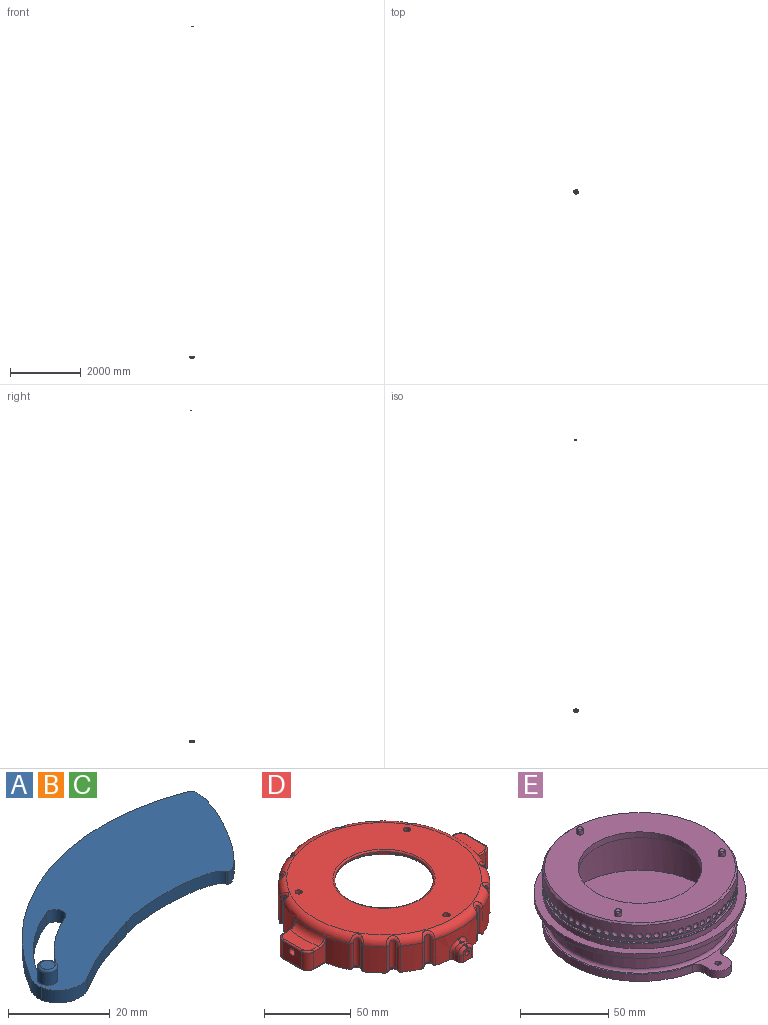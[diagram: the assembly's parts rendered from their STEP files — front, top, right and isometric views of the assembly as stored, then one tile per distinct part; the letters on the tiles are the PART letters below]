
ASSEMBLY  parts=5 mates=6
PART A: 17 faces, bbox 68.7x35.4x6.5 mm
  f0: extruded ~26.08x3.35mm, area 81.3mm2, adj f3,f4,f8,f16
  f1: extruded ~24.8x14.67mm, area 90.9mm2, adj f2,f3,f4,f8
  f2: cylinder r=54.5mm len=67.29mm, axis (0,0,-1), area 232.4mm2, adj f1,f3,f4,f14
  f3: plane 68.73x35.38mm, normal (0,0,1), area 1340.6mm2, adj f0,f1,f2,f5,f7,f8,f9,f10
  f4: plane 68.73x35.38mm, normal (0,0,-1), area 1353.2mm2, adj f0,f1,f2,f7,f8,f9,f10,f11
  f5: cylinder r=2mm len=4mm, axis (0,0,-1), area 37.7mm2, adj f3,f13
  f6: plane 3x3mm, normal (0,0,1), area 7.1mm2, adj f13
  f7: extruded ~14.32x6.42mm, area 47.2mm2, adj f3,f4,f15,f16
  f8: cylinder r=0.3mm len=3mm, axis (0,0,-1), area 1mm2, adj f0,f1,f3,f4
  f9: cylinder r=32.5mm len=14.49mm, axis (0,0,1), area 56.5mm2, adj f3,f4,f10,f12
  f10: cylinder r=2.05mm len=3.74mm, axis (0,0,1), area 19.3mm2, adj f3,f4,f9,f11
  f11: cylinder r=28.4mm len=12.66mm, axis (0,0,1), area 49.4mm2, adj f3,f4,f10,f12
  f12: cylinder r=2.05mm len=3.95mm, axis (0,0,1), area 19.3mm2, adj f3,f4,f9,f11
  f13: torus R=1.5mm, axis (0,0,1), area 9mm2, adj f5,f6
  f14: cylinder r=6mm len=3.7mm, axis (0,0,-1), area 11.6mm2, adj f2,f3,f4,f15
  f15: cylinder r=6mm len=9.02mm, axis (0,0,1), area 34.5mm2, adj f3,f4,f7,f14
  f16: cylinder r=60mm len=4.4mm, axis (0,0,-1), area 13.9mm2, adj f0,f3,f4,f7
PART B: same geometry as A
PART C: same geometry as A
PART D: 203 faces, bbox 150.8x136x23.4 mm
  f0: cylinder r=2.15mm len=12.4mm, axis (1,0,0), area 167.5mm2, adj f31,f172
  f1: plane 53.71x23.5mm, normal (0,0,-1), area 489.7mm2, adj f21,f28,f34,f107,f122,f162,f163,f166
  f2: cylinder r=2.15mm len=12.4mm, axis (1,0,0), area 167.5mm2, adj f31,f166
  f3: plane 53.71x23.5mm, normal (0,0,-1), area 489.7mm2, adj f15,f27,f34,f137,f152,f168,f171,f172
  f4: plane 13.56x12.34mm, normal (0,0,-1), area 52.7mm2, adj f8,f34,f148,f152
  f5: plane 14.36x10.74mm, normal (0,0,-1), area 52.7mm2, adj f7,f34,f144,f148
  f6: cylinder r=61.2mm len=34.07mm, axis (0,0,-1), area 481mm2, adj f12,f18,f71,f72,f73,f74,f75,f114
  f7: cylinder r=61.2mm len=18.4mm, axis (0,0,-1), area 242.2mm2, adj f5,f12,f144,f145,f148,f150
  f8: cylinder r=61.2mm len=18.4mm, axis (0,0,-1), area 242.2mm2, adj f4,f12,f148,f149,f152,f154
  f9: plane 13.56x12.34mm, normal (0,0,-1), area 52.7mm2, adj f14,f34,f133,f137
  f10: plane 14.36x10.74mm, normal (0,0,-1), area 52.7mm2, adj f13,f34,f129,f133
  f11: plane 35.36x13.6mm, normal (0,0,-1), area 196.5mm2, adj f23,f34,f39,f40,f41,f45,f46,f49
  f12: torus R=56.2mm, axis (0,0,1), area 2369.6mm2, adj f6,f7,f8,f13,f14,f15,f19,f20
  f13: cylinder r=61.2mm len=18.4mm, axis (0,0,-1), area 242.2mm2, adj f10,f12,f129,f130,f133,f135
  f14: cylinder r=61.2mm len=18.4mm, axis (0,0,-1), area 242.2mm2, adj f9,f12,f133,f134,f137,f139
  f15: cylinder r=61.2mm len=18.4mm, axis (0,0,-1), area 283.5mm2, adj f3,f12,f82,f137,f138,f180,f185
  f16: plane 13.56x12.34mm, normal (0,0,-1), area 52.7mm2, adj f20,f34,f118,f122
  f17: plane 14.36x10.74mm, normal (0,0,-1), area 52.7mm2, adj f19,f34,f114,f118
  f18: plane 35.36x13.6mm, normal (0,0,-1), area 196.5mm2, adj f6,f34,f35,f36,f37,f63,f64,f67
  f19: cylinder r=61.2mm len=18.4mm, axis (0,0,-1), area 242.2mm2, adj f12,f17,f114,f115,f118,f120
  f20: cylinder r=61.2mm len=18.4mm, axis (0,0,-1), area 242.2mm2, adj f12,f16,f118,f119,f122,f124
  f21: cylinder r=61.2mm len=18.4mm, axis (0,0,-1), area 283.5mm2, adj f1,f12,f87,f122,f123,f186,f191
  f22: plane 13.56x12.34mm, normal (0,0,-1), area 52.7mm2, adj f25,f34,f103,f107
  f23: cylinder r=61.2mm len=34.07mm, axis (0,0,-1), area 481mm2, adj f11,f12,f53,f54,f55,f56,f57,f99
  f24: cylinder r=61.2mm len=18.4mm, axis (0,0,-1), area 242.2mm2, adj f12,f26,f99,f100,f103,f105
  f25: cylinder r=61.2mm len=18.4mm, axis (0,0,-1), area 242.2mm2, adj f12,f22,f103,f104,f107,f109
  f26: plane 14.36x10.74mm, normal (0,0,-1), area 52.7mm2, adj f24,f34,f99,f103
  f27: cylinder r=61.2mm len=18.4mm, axis (0,0,-1), area 283.5mm2, adj f3,f12,f84,f152,f153,f174,f181
  f28: cylinder r=61.2mm len=18.4mm, axis (0,0,-1), area 283.5mm2, adj f1,f12,f86,f107,f108,f190,f197
  f29: cylinder r=1.75mm len=6.3mm, axis (0,-1,0), area 69.3mm2, adj f31,f67
  f30: cylinder r=1.75mm len=6.3mm, axis (0,-1,0), area 69.3mm2, adj f31,f49
  f31: cylinder r=55.2mm len=110.4mm, axis (0,0,-1), area 6264mm2, adj f0,f2,f29,f30,f34,f81
  f32: plane 110x110mm, normal (0,0,-1), area 6705.6mm2, adj f81,f198,f200,f201,f202
  f33: plane 112.4x112.4mm, normal (0,0,1), area 7147mm2, adj f12,f157,f158,f159,f199
  f34: cone r=57.2mm half-angle=45deg, axis (0,0,-1), area 998.8mm2, adj f1,f3,f4,f5,f9,f10,f11,f16
  f35: plane 5x3.25mm, normal (-1,0,0), area 16.2mm2, adj f18,f70,f75,f80
  f36: plane 5x3.25mm, normal (1,0,0), area 16.2mm2, adj f18,f69,f71,f76
  f37: plane 8x7mm, normal (0,1,0), area 42.5mm2, adj f18,f44,f76,f77,f78,f79,f80
  f38: plane 2.8x1mm, normal (0,0,1), area 2.8mm2, adj f69,f70,f73,f78
  f39: plane 5x3.25mm, normal (-1,0,0), area 16.2mm2, adj f11,f52,f57,f58
  f40: plane 8x7mm, normal (0,-1,0), area 42.5mm2, adj f11,f43,f58,f59,f60,f61,f62
  f41: plane 5x3.25mm, normal (1,0,0), area 16.2mm2, adj f11,f51,f53,f62
  f42: plane 2.8x1mm, normal (0,0,1), area 2.8mm2, adj f51,f52,f55,f60
  f43: cylinder r=1.75mm len=4mm, axis (0,-1,0), area 44mm2, adj f40,f50
  f44: cylinder r=1.75mm len=4mm, axis (0,-1,0), area 44mm2, adj f37,f68
  f45: plane 6.63x2.5mm, normal (1,0,0), area 16.6mm2, adj f11,f48,f49,f50
  f46: plane 6.63x2.5mm, normal (-1,0,0), area 16.6mm2, adj f11,f47,f49,f50
  f47: plane 2.83x2.5mm, normal (-0.5,0,-0.87), area 8.2mm2, adj f46,f48,f49,f50
  f48: plane 2.83x2.5mm, normal (0.5,0,-0.87), area 8.2mm2, adj f45,f47,f49,f50
  f49: plane 8.26x5.65mm, normal (0,-1,0), area 32.5mm2, adj f11,f30,f45,f46,f47,f48
  f50: plane 8.26x5.65mm, normal (0,1,0), area 32.5mm2, adj f11,f43,f45,f46,f47,f48
  f51: cylinder r=5mm len=5mm, axis (0,-1,0), area 23.8mm2, adj f41,f42,f54,f61
  f52: cylinder r=5mm len=5mm, axis (0,1,0), area 23.8mm2, adj f39,f42,f56,f59
  f53: cylinder r=2mm len=5mm, axis (0,0,-1), area 14.5mm2, adj f11,f23,f41,f54
  f54: bspline ~8.56x8.28mm, area 27mm2, adj f23,f51,f53,f55
  f55: torus R=63.2mm, axis (0,0,1), area 3.1mm2, adj f23,f42,f54,f56
  f56: bspline ~8.56x8.28mm, area 27mm2, adj f23,f52,f55,f57
  f57: cylinder r=2mm len=5mm, axis (0,0,-1), area 14.5mm2, adj f11,f23,f39,f56
  f58: cylinder r=2mm len=5mm, axis (0,0,1), area 15.7mm2, adj f11,f39,f40,f59
  f59: torus R=3mm, axis (0,1,0), area 21.1mm2, adj f40,f52,f58,f60
  f60: cylinder r=2mm len=2mm, axis (-1,0,0), area 3.1mm2, adj f40,f42,f59,f61
  f61: torus R=3mm, axis (0,1,0), area 21.1mm2, adj f40,f51,f60,f62
  f62: cylinder r=2mm len=5mm, axis (0,0,-1), area 15.7mm2, adj f11,f40,f41,f61
  f63: plane 6.63x2.5mm, normal (-1,0,0), area 16.6mm2, adj f18,f66,f67,f68
  f64: plane 6.63x2.5mm, normal (1,0,0), area 16.6mm2, adj f18,f65,f67,f68
  f65: plane 2.83x2.5mm, normal (0.5,0,-0.87), area 8.2mm2, adj f64,f66,f67,f68
  f66: plane 2.83x2.5mm, normal (-0.5,0,-0.87), area 8.2mm2, adj f63,f65,f67,f68
  f67: plane 8.26x5.65mm, normal (0,1,0), area 32.5mm2, adj f18,f29,f63,f64,f65,f66
  f68: plane 8.26x5.65mm, normal (0,-1,0), area 32.5mm2, adj f18,f44,f63,f64,f65,f66
  f69: cylinder r=5mm len=5mm, axis (0,-1,0), area 23.8mm2, adj f36,f38,f72,f77
  f70: cylinder r=5mm len=5mm, axis (0,1,0), area 23.8mm2, adj f35,f38,f74,f79
  f71: cylinder r=2mm len=5mm, axis (0,0,-1), area 14.5mm2, adj f6,f18,f36,f72
  f72: bspline ~8.28x7.4mm, area 27mm2, adj f6,f69,f71,f73
  f73: torus R=63.2mm, axis (0,0,1), area 3.1mm2, adj f6,f38,f72,f74
  f74: bspline ~8.56x8.28mm, area 27mm2, adj f6,f70,f73,f75
  f75: cylinder r=2mm len=5mm, axis (0,0,-1), area 14.5mm2, adj f6,f18,f35,f74
  f76: cylinder r=2mm len=5mm, axis (0,0,1), area 15.7mm2, adj f18,f36,f37,f77
  f77: torus R=3mm, axis (0,1,0), area 21.1mm2, adj f37,f69,f76,f78
  f78: cylinder r=2mm len=2mm, axis (1,0,0), area 3.1mm2, adj f37,f38,f77,f79
  f79: torus R=3mm, axis (0,1,0), area 21.1mm2, adj f37,f70,f78,f80
  f80: cylinder r=2mm len=5mm, axis (0,0,-1), area 15.7mm2, adj f18,f35,f37,f79
  f81: cone r=55.2mm half-angle=45deg, axis (0,0,-1), area 97.9mm2, adj f31,f32
  f82: plane 14.97x10.09mm, normal (0,-1,0), area 125.6mm2, adj f15,f93,f179,f180,f185
  f83: plane 15x12mm, normal (-1,0,0), area 165.5mm2, adj f92,f93,f161,f177,f183
  f84: plane 14.97x10.09mm, normal (0,1,0), area 125.6mm2, adj f27,f92,f174,f175,f181
  f85: plane 23x8.83mm, normal (0,0,1), area 180.6mm2, adj f95,f175,f176,f177,f178,f179
  f86: plane 14.97x10.09mm, normal (0,-1,0), area 125.6mm2, adj f28,f91,f190,f196,f197
  f87: plane 14.97x10.09mm, normal (0,1,0), area 125.6mm2, adj f21,f90,f186,f191,f192
  f88: plane 15x12mm, normal (1,0,0), area 165.5mm2, adj f90,f91,f160,f188,f194
  f89: plane 23x8.83mm, normal (0,0,1), area 180.6mm2, adj f94,f192,f193,f194,f195,f196
  f90: cylinder r=5mm len=12mm, axis (0,0,1), area 94.2mm2, adj f87,f88,f187,f193
  f91: cylinder r=5mm len=12mm, axis (0,0,-1), area 94.2mm2, adj f86,f88,f189,f195
  f92: cylinder r=5mm len=12mm, axis (0,0,-1), area 94.2mm2, adj f83,f84,f176,f182
  f93: cylinder r=5mm len=12mm, axis (0,0,1), area 94.2mm2, adj f82,f83,f178,f184
  f94: torus R=66.18mm, axis (0,0,-1), area 174.7mm2, adj f12,f89,f191,f197
  f95: torus R=66.18mm, axis (0,0,-1), area 174.7mm2, adj f12,f85,f174,f180
  f96: cylinder r=2.5mm len=19.36mm, axis (0,0,-1), area 101.7mm2, adj f107,f108,f109,f110
  f97: cylinder r=2.5mm len=19.36mm, axis (0,0,-1), area 101.7mm2, adj f103,f104,f105,f106
  f98: cylinder r=2.5mm len=19.36mm, axis (0,0,-1), area 101.7mm2, adj f99,f100,f101,f102
  f99: torus R=4.5mm, axis (0,0,1), area 27.7mm2, adj f11,f23,f24,f26,f34,f98,f100,f101
  f100: cylinder r=2mm len=18.36mm, axis (0,0,1), area 39.8mm2, adj f24,f98,f99,f102
  f101: cylinder r=2mm len=18.36mm, axis (0,0,1), area 39.8mm2, adj f23,f98,f99,f102
  f102: bspline ~7.7x5.94mm, area 31.7mm2, adj f12,f98,f100,f101
  f103: torus R=4.5mm, axis (0,0,1), area 27.7mm2, adj f22,f24,f25,f26,f34,f97,f104,f105
  f104: cylinder r=2mm len=18.36mm, axis (0,0,1), area 39.8mm2, adj f25,f97,f103,f106
  f105: cylinder r=2mm len=18.36mm, axis (0,0,1), area 39.8mm2, adj f24,f97,f103,f106
  f106: bspline ~6.84x6.41mm, area 31.7mm2, adj f12,f97,f104,f105
  f107: torus R=4.5mm, axis (0,0,1), area 27.7mm2, adj f1,f22,f25,f28,f34,f96,f108,f109
  f108: cylinder r=2mm len=18.36mm, axis (0,0,1), area 39.8mm2, adj f28,f96,f107,f110
  f109: cylinder r=2mm len=18.36mm, axis (0,0,1), area 39.8mm2, adj f25,f96,f107,f110
  f110: bspline ~7.26x5.94mm, area 31.7mm2, adj f12,f96,f108,f109
  f111: cylinder r=2.5mm len=19.36mm, axis (0,0,-1), area 101.7mm2, adj f122,f123,f124,f125
  f112: cylinder r=2.5mm len=19.36mm, axis (0,0,-1), area 101.7mm2, adj f118,f119,f120,f121
  f113: cylinder r=2.5mm len=19.36mm, axis (0,0,-1), area 101.7mm2, adj f114,f115,f116,f117
  f114: torus R=4.5mm, axis (0,0,1), area 27.7mm2, adj f6,f17,f18,f19,f34,f113,f115,f116
  f115: cylinder r=2mm len=18.36mm, axis (0,0,1), area 39.8mm2, adj f19,f113,f114,f117
  f116: cylinder r=2mm len=18.36mm, axis (0,0,1), area 39.8mm2, adj f6,f113,f114,f117
  f117: bspline ~7.7x5.93mm, area 31.7mm2, adj f12,f113,f115,f116
  f118: torus R=4.5mm, axis (0,0,1), area 27.7mm2, adj f16,f17,f19,f20,f34,f112,f119,f120
  f119: cylinder r=2mm len=18.36mm, axis (0,0,1), area 39.8mm2, adj f20,f112,f118,f121
  f120: cylinder r=2mm len=18.36mm, axis (0,0,1), area 39.8mm2, adj f19,f112,f118,f121
  f121: bspline ~6.85x6.41mm, area 31.7mm2, adj f12,f112,f119,f120
  f122: torus R=4.5mm, axis (0,0,1), area 27.7mm2, adj f1,f16,f20,f21,f34,f111,f123,f124
  f123: cylinder r=2mm len=18.36mm, axis (0,0,1), area 39.8mm2, adj f21,f111,f122,f125
  f124: cylinder r=2mm len=18.36mm, axis (0,0,1), area 39.8mm2, adj f20,f111,f122,f125
  f125: bspline ~7.26x5.94mm, area 31.7mm2, adj f12,f111,f123,f124
  f126: cylinder r=2.5mm len=19.36mm, axis (0,0,-1), area 101.7mm2, adj f137,f138,f139,f140
  f127: cylinder r=2.5mm len=19.36mm, axis (0,0,-1), area 101.7mm2, adj f133,f134,f135,f136
  f128: cylinder r=2.5mm len=19.36mm, axis (0,0,-1), area 101.7mm2, adj f129,f130,f131,f132
  f129: torus R=4.5mm, axis (0,0,1), area 27.7mm2, adj f10,f11,f13,f23,f34,f128,f130,f131
  f130: cylinder r=2mm len=18.36mm, axis (0,0,1), area 39.8mm2, adj f13,f128,f129,f132
  f131: cylinder r=2mm len=18.36mm, axis (0,0,1), area 39.8mm2, adj f23,f128,f129,f132
  f132: bspline ~7.7x5.93mm, area 31.7mm2, adj f12,f128,f130,f131
  f133: torus R=4.5mm, axis (0,0,1), area 27.7mm2, adj f9,f10,f13,f14,f34,f127,f134,f135
  f134: cylinder r=2mm len=18.36mm, axis (0,0,1), area 39.8mm2, adj f14,f127,f133,f136
  f135: cylinder r=2mm len=18.36mm, axis (0,0,1), area 39.8mm2, adj f13,f127,f133,f136
  f136: bspline ~6.85x6.41mm, area 31.7mm2, adj f12,f127,f134,f135
  f137: torus R=4.5mm, axis (0,0,1), area 27.7mm2, adj f3,f9,f14,f15,f34,f126,f138,f139
  f138: cylinder r=2mm len=18.36mm, axis (0,0,1), area 39.8mm2, adj f15,f126,f137,f140
  f139: cylinder r=2mm len=18.36mm, axis (0,0,1), area 39.8mm2, adj f14,f126,f137,f140
  f140: bspline ~7.26x5.93mm, area 31.7mm2, adj f12,f126,f138,f139
  f141: cylinder r=2.5mm len=19.36mm, axis (0,0,-1), area 101.7mm2, adj f152,f153,f154,f155
  f142: cylinder r=2.5mm len=19.36mm, axis (0,0,-1), area 101.7mm2, adj f148,f149,f150,f151
  f143: cylinder r=2.5mm len=19.36mm, axis (0,0,-1), area 101.7mm2, adj f144,f145,f146,f147
  f144: torus R=4.5mm, axis (0,0,1), area 27.7mm2, adj f5,f6,f7,f18,f34,f143,f145,f146
  f145: cylinder r=2mm len=18.36mm, axis (0,0,1), area 39.8mm2, adj f7,f143,f144,f147
  f146: cylinder r=2mm len=18.36mm, axis (0,0,1), area 39.8mm2, adj f6,f143,f144,f147
  f147: bspline ~7.7x5.94mm, area 31.7mm2, adj f12,f143,f145,f146
  f148: torus R=4.5mm, axis (0,0,1), area 27.7mm2, adj f4,f5,f7,f8,f34,f142,f149,f150
  f149: cylinder r=2mm len=18.36mm, axis (0,0,1), area 39.8mm2, adj f8,f142,f148,f151
  f150: cylinder r=2mm len=18.36mm, axis (0,0,1), area 39.8mm2, adj f7,f142,f148,f151
  f151: bspline ~6.84x6.41mm, area 31.7mm2, adj f12,f142,f149,f150
  f152: torus R=4.5mm, axis (0,0,1), area 27.7mm2, adj f3,f4,f8,f27,f34,f141,f153,f154
  f153: cylinder r=2mm len=18.36mm, axis (0,0,1), area 39.8mm2, adj f27,f141,f152,f155
  f154: cylinder r=2mm len=18.36mm, axis (0,0,1), area 39.8mm2, adj f8,f141,f152,f155
  f155: bspline ~7.26x5.94mm, area 31.7mm2, adj f12,f141,f153,f154
  f156: cylinder r=28.5mm len=57mm, axis (0,0,1), area 179.1mm2, adj f198,f199
  f157: cylinder r=2.1mm len=4.2mm, axis (0,0,1), area 33mm2, adj f33,f202
  f158: cylinder r=2.1mm len=4.2mm, axis (0,0,1), area 33mm2, adj f33,f200
  f159: cylinder r=2.1mm len=4.2mm, axis (0,0,1), area 33mm2, adj f33,f201
  f160: cylinder r=2.15mm len=4.3mm, axis (1,0,0), area 54mm2, adj f88,f167
  f161: cylinder r=2.15mm len=4.3mm, axis (1,0,0), area 54mm2, adj f83,f173
  f162: plane 11.05x3.4mm, normal (0,1,0), area 37.6mm2, adj f1,f165,f166,f167
  f163: plane 11.05x3.4mm, normal (0,-1,0), area 37.6mm2, adj f1,f164,f166,f167
  f164: plane 3.55x3.4mm, normal (0,-0.5,-0.87), area 13.9mm2, adj f163,f165,f166,f167
  f165: plane 3.55x3.4mm, normal (0,0.5,-0.87), area 13.9mm2, adj f162,f164,f166,f167
  f166: plane 13.1x7.1mm, normal (1,0,0), area 71.2mm2, adj f1,f2,f162,f163,f164,f165
  f167: plane 13.1x7.1mm, normal (-1,0,0), area 71.2mm2, adj f1,f160,f162,f163,f164,f165
  f168: plane 11.05x3.4mm, normal (0,1,0), area 37.6mm2, adj f3,f169,f172,f173
  f169: plane 3.55x3.4mm, normal (0,0.5,-0.87), area 13.9mm2, adj f168,f170,f172,f173
  f170: plane 3.55x3.4mm, normal (0,-0.5,-0.87), area 13.9mm2, adj f169,f171,f172,f173
  f171: plane 11.05x3.4mm, normal (0,-1,0), area 37.6mm2, adj f3,f170,f172,f173
  f172: plane 13.1x7.1mm, normal (-1,0,0), area 71.2mm2, adj f0,f3,f168,f169,f170,f171
  f173: plane 13.1x7.1mm, normal (1,0,0), area 71.2mm2, adj f3,f161,f168,f169,f170,f171
  f174: bspline ~7.48x6.11mm, area 10.2mm2, adj f12,f27,f84,f95,f175
  f175: cylinder r=1mm len=4.83mm, axis (-1,0,0), area 7.6mm2, adj f84,f85,f174,f176
  f176: torus R=4mm, axis (0,0,-1), area 11.4mm2, adj f85,f92,f175,f177
  f177: cylinder r=1mm len=15mm, axis (0,-1,0), area 23.6mm2, adj f83,f85,f176,f178
  f178: torus R=4mm, axis (0,0,-1), area 11.4mm2, adj f85,f93,f177,f179
  f179: cylinder r=1mm len=4.83mm, axis (1,0,0), area 7.6mm2, adj f82,f85,f178,f180
  f180: bspline ~7.48x6.11mm, area 10.2mm2, adj f12,f15,f82,f95,f179
  f181: cylinder r=1mm len=10.09mm, axis (-1,0,0), area 15.7mm2, adj f3,f27,f84,f182
  f182: torus R=4mm, axis (0,0,1), area 11.4mm2, adj f3,f92,f181,f183
  f183: cylinder r=1mm len=15mm, axis (0,-1,0), area 23.6mm2, adj f3,f83,f182,f184
  f184: torus R=4mm, axis (0,0,1), area 11.4mm2, adj f3,f93,f183,f185
  f185: cylinder r=1mm len=10.09mm, axis (1,0,0), area 15.7mm2, adj f3,f15,f82,f184
  f186: cylinder r=1mm len=10.09mm, axis (-1,0,0), area 15.7mm2, adj f1,f21,f87,f187
  f187: torus R=4mm, axis (0,0,1), area 11.4mm2, adj f1,f90,f186,f188
  f188: cylinder r=1mm len=15mm, axis (0,1,0), area 23.6mm2, adj f1,f88,f187,f189
  f189: torus R=4mm, axis (0,0,1), area 11.4mm2, adj f1,f91,f188,f190
  f190: cylinder r=1mm len=10.09mm, axis (1,0,0), area 15.7mm2, adj f1,f28,f86,f189
  f191: bspline ~7.48x6.11mm, area 10.2mm2, adj f12,f21,f87,f94,f192
  f192: cylinder r=1mm len=4.83mm, axis (-1,0,0), area 7.6mm2, adj f87,f89,f191,f193
  f193: torus R=4mm, axis (0,0,-1), area 11.4mm2, adj f89,f90,f192,f194
  f194: cylinder r=1mm len=15mm, axis (0,1,0), area 23.6mm2, adj f88,f89,f193,f195
  f195: torus R=4mm, axis (0,0,-1), area 11.4mm2, adj f89,f91,f194,f196
  f196: cylinder r=1mm len=4.83mm, axis (1,0,0), area 7.6mm2, adj f86,f89,f195,f197
  f197: bspline ~7.48x6.11mm, area 10.2mm2, adj f12,f28,f86,f94,f196
  f198: torus R=29.5mm, axis (0,0,1), area 284.9mm2, adj f32,f156
  f199: torus R=29.5mm, axis (0,0,1), area 284.9mm2, adj f33,f156
  f200: cone r=2.6mm half-angle=45deg, axis (0,0,-1), area 10.4mm2, adj f32,f158
  f201: cone r=2.6mm half-angle=45deg, axis (0,0,-1), area 10.4mm2, adj f32,f159
  f202: cone r=2.6mm half-angle=45deg, axis (0,0,-1), area 10.4mm2, adj f32,f157
PART E: 116 faces, bbox 120x140x43.2 mm
  f0: plane 108x108mm, normal (0,0,1), area 5274.7mm2, adj f8,f103,f106,f109,f112
  f1: cylinder r=55mm len=110mm, axis (0,0,-1), area 1226.8mm2, adj f4,f10
  f2: cylinder r=60mm len=120mm, axis (0,0,1), area 1131mm2, adj f3,f4
  f3: plane 120x120mm, normal (0,0,-1), area 2148.8mm2, adj f2,f29
  f4: plane 120x120mm, normal (0,0,1), area 1806.4mm2, adj f1,f2
  f5: plane 109.6x109.6mm, normal (0,0,-1), area 358.1mm2, adj f6,f11
  f6: cylinder r=53.75mm len=107.5mm, axis (0,0,1), area 844.3mm2, adj f5,f7
  f7: plane 109.6x109.6mm, normal (0,0,1), area 358.1mm2, adj f6,f10
  f8: cone r=54mm half-angle=45deg, axis (0,0,-1), area 484.3mm2, adj f0,f9
  f9: cylinder r=55mm len=110mm, axis (0,0,-1), area 2746.1mm2, adj f8,f11,f31,f32,f33,f34,f35,f36
  f10: cone r=54.8mm half-angle=45deg, axis (0,0,-1), area 97.6mm2, adj f1,f7
  f11: cone r=55mm half-angle=45deg, axis (0,0,1), area 97.6mm2, adj f5,f9
  f12: cylinder r=52mm len=104mm, axis (0,0,-1), area 3463.3mm2, adj f29,f30
  f13: plane 5x3.82mm, normal (-1,0,0), area 19.1mm2, adj f14,f17,f25,f26
  f14: cylinder r=7.5mm len=15mm, axis (0,0,-1), area 117.8mm2, adj f13,f15,f25,f26
  f15: plane 5x3.82mm, normal (1,0,0), area 19.1mm2, adj f14,f23,f25,f26
  f16: cylinder r=1.75mm len=5mm, axis (0,0,-1), area 55mm2, adj f25,f26
  f17: cylinder r=5mm len=5mm, axis (0,0,-1), area 34mm2, adj f13,f24,f25,f26
  f18: cylinder r=5mm len=5mm, axis (0,0,-1), area 34mm2, adj f21,f24,f25,f26
  f19: plane 5x3.82mm, normal (1,0,0), area 19.1mm2, adj f20,f25,f26,f27
  f20: cylinder r=7.5mm len=15mm, axis (0,0,-1), area 117.8mm2, adj f19,f21,f25,f26
  f21: plane 5x3.82mm, normal (-1,0,0), area 19.1mm2, adj f18,f20,f25,f26
  f22: cylinder r=1.75mm len=5mm, axis (0,0,-1), area 55mm2, adj f25,f26
  f23: cylinder r=5mm len=5mm, axis (0,0,-1), area 34mm2, adj f15,f25,f26,f28
  f24: cylinder r=55mm len=107.59mm, axis (0,0,-1), area 748.5mm2, adj f17,f18,f25,f26
  f25: plane 140x110mm, normal (0,0,-1), area 9904.6mm2, adj f13,f14,f15,f16,f17,f18,f19,f20
  f26: plane 140x110mm, normal (0,0,1), area 743.7mm2, adj f13,f14,f15,f16,f17,f18,f19,f20
  f27: cylinder r=5mm len=5mm, axis (0,0,-1), area 34mm2, adj f19,f25,f26,f28
  f28: cylinder r=55mm len=107.59mm, axis (0,0,-1), area 748.5mm2, adj f23,f25,f26,f27
  f29: torus R=54mm, axis (0,0,-1), area 1040.8mm2, adj f3,f12
  f30: torus R=54mm, axis (0,0,-1), area 1040.8mm2, adj f12,f26
  f31: sphere r=1.75mm, area 19.1mm2, adj f9
  f32: sphere r=1.75mm, area 19.1mm2, adj f9
  f33: sphere r=1.75mm, area 20.8mm2, adj f9
  f34: sphere r=1.75mm, area 19.1mm2, adj f9
  f35: sphere r=1.75mm, area 19.2mm2, adj f9
  f36: sphere r=1.75mm, area 20.8mm2, adj f9
  f37: sphere r=1.75mm, area 19.1mm2, adj f9
  f38: sphere r=1.75mm, area 20.8mm2, adj f9
  f39: sphere r=1.75mm, area 19.2mm2, adj f9
  f40: sphere r=1.75mm, area 20.8mm2, adj f9
  f41: sphere r=1.75mm, area 19.2mm2, adj f9
  f42: sphere r=1.75mm, area 20.8mm2, adj f9
  f43: sphere r=1.75mm, area 20.8mm2, adj f9
  f44: sphere r=1.75mm, area 19.1mm2, adj f9
  f45: sphere r=1.75mm, area 19.1mm2, adj f9
  f46: sphere r=1.75mm, area 20.8mm2, adj f9
  f47: sphere r=1.75mm, area 20.8mm2, adj f9
  f48: sphere r=1.75mm, area 19.1mm2, adj f9
  f49: sphere r=1.75mm, area 19.1mm2, adj f9
  f50: sphere r=1.75mm, area 19.1mm2, adj f9
  f51: sphere r=1.75mm, area 20.8mm2, adj f9
  f52: sphere r=1.75mm, area 19.1mm2, adj f9
  f53: sphere r=1.75mm, area 19.2mm2, adj f9
  f54: sphere r=1.75mm, area 20.8mm2, adj f9
  f55: sphere r=1.75mm, area 19.1mm2, adj f9
  f56: sphere r=1.75mm, area 20.8mm2, adj f9
  f57: sphere r=1.75mm, area 19.2mm2, adj f9
  f58: sphere r=1.75mm, area 20.8mm2, adj f9
  f59: sphere r=1.75mm, area 19.2mm2, adj f9
  f60: sphere r=1.75mm, area 20.8mm2, adj f9
  f61: sphere r=1.75mm, area 20.8mm2, adj f9
  f62: sphere r=1.75mm, area 19.1mm2, adj f9
  f63: sphere r=1.75mm, area 19.1mm2, adj f9
  f64: sphere r=1.75mm, area 20.8mm2, adj f9
  f65: sphere r=1.75mm, area 20.8mm2, adj f9
  f66: sphere r=1.75mm, area 19.1mm2, adj f9
  f67: sphere r=1.75mm, area 19.1mm2, adj f9
  f68: sphere r=1.75mm, area 19.1mm2, adj f9
  f69: sphere r=1.75mm, area 20.8mm2, adj f9
  f70: sphere r=1.75mm, area 20.8mm2, adj f9
  f71: sphere r=1.75mm, area 19.1mm2, adj f9
  f72: sphere r=1.75mm, area 19.1mm2, adj f9
  f73: sphere r=1.75mm, area 20.8mm2, adj f9
  f74: sphere r=1.75mm, area 20.8mm2, adj f9
  f75: sphere r=1.75mm, area 19.2mm2, adj f9
  f76: sphere r=1.75mm, area 20.8mm2, adj f9
  f77: sphere r=1.75mm, area 19.2mm2, adj f9
  f78: sphere r=1.75mm, area 20.8mm2, adj f9
  f79: sphere r=1.75mm, area 19.1mm2, adj f9
  f80: sphere r=1.75mm, area 20.8mm2, adj f9
  f81: sphere r=1.75mm, area 19.2mm2, adj f9
  f82: sphere r=1.75mm, area 20.8mm2, adj f9
  f83: sphere r=1.75mm, area 20.8mm2, adj f9
  f84: sphere r=1.75mm, area 19.1mm2, adj f9
  f85: sphere r=1.75mm, area 19.1mm2, adj f9
  f86: sphere r=1.75mm, area 19.1mm2, adj f9
  f87: sphere r=1.75mm, area 20.8mm2, adj f9
  f88: sphere r=1.75mm, area 20.8mm2, adj f9
  f89: sphere r=1.75mm, area 19.1mm2, adj f9
  f90: sphere r=1.75mm, area 19.1mm2, adj f9
  f91: sphere r=1.75mm, area 20.8mm2, adj f9
  f92: sphere r=1.75mm, area 20.8mm2, adj f9
  f93: sphere r=1.75mm, area 19.2mm2, adj f9
  f94: sphere r=1.75mm, area 20.8mm2, adj f9
  f95: sphere r=1.75mm, area 19.2mm2, adj f9
  f96: sphere r=1.75mm, area 20.8mm2, adj f9
  f97: sphere r=1.75mm, area 19.1mm2, adj f9
  f98: sphere r=1.75mm, area 20.8mm2, adj f9
  f99: sphere r=1.75mm, area 19.2mm2, adj f9
  f100: sphere r=1.75mm, area 19.1mm2, adj f9
  f101: sphere r=1.75mm, area 20.8mm2, adj f9
  f102: sphere r=1.75mm, area 19.1mm2, adj f9
  f103: cylinder r=2mm len=4mm, axis (0,0,-1), area 33.9mm2, adj f0,f105
  f104: plane 3x3mm, normal (0,0,1), area 7.1mm2, adj f105
  f105: cone r=1.5mm half-angle=45deg, axis (0,0,-1), area 7.8mm2, adj f103,f104
  f106: cylinder r=2mm len=4mm, axis (0,0,-1), area 33.9mm2, adj f0,f108
  f107: plane 3x3mm, normal (0,0,1), area 7.1mm2, adj f108
  f108: cone r=1.5mm half-angle=45deg, axis (0,0,-1), area 7.8mm2, adj f106,f107
  f109: cylinder r=2mm len=4mm, axis (0,0,-1), area 33.9mm2, adj f0,f111
  f110: plane 3x3mm, normal (0,0,1), area 7.1mm2, adj f111
  f111: cone r=1.5mm half-angle=45deg, axis (0,0,-1), area 7.8mm2, adj f109,f110
  f112: cylinder r=35mm len=70mm, axis (0,0,1), area 879.6mm2, adj f0,f113
  f113: plane 94x94mm, normal (0,0,-1), area 3091.3mm2, adj f112,f115
  f114: plane 94x94mm, normal (0,0,1), area 6939.8mm2, adj f115
  f115: cylinder r=47mm len=94mm, axis (0,0,-1), area 9154.6mm2, adj f113,f114
PLACE A rot(axis=(0,0,-1),41.2deg) t=(38.17,20.16,9356.82)mm
PLACE B rot(axis=(0,0,-1),161.5deg) t=(20.58,-18.58,46.5)mm
PLACE C rot(axis=(0,0,1),78.8deg) t=(-4.35,15.81,46.5)mm
PLACE D rot(axis=(0,0,-1),38.2deg) t=(18.16,5.71,29.1)mm
PLACE E t=(18.16,5.71,11.5)mm fixed
MATE cylindrical B.f5 <-> D.f158  axis (0,0,1) through (68.65,-1.53,52.85)mm
MATE planar B.f4 <-> E.f6  axis (0,0,-1) through (17.74,-32.54,46.5)mm
MATE cylindrical D.f157 <-> C.f5  axis (0,0,1) through (-13.35,-34.39,51.25)mm
MATE revolute D.f31 <-> E.f2  axis (0,0,-1) through (18.16,5.71,29.1)mm
MATE planar C.f4 <-> E.f6  axis (0,0,-1) through (-20.2,2.09,46.5)mm
MATE cylindrical D.f159 <-> A.f5  axis (0,0,1) through (-0.81,53.05,52.5)mm
